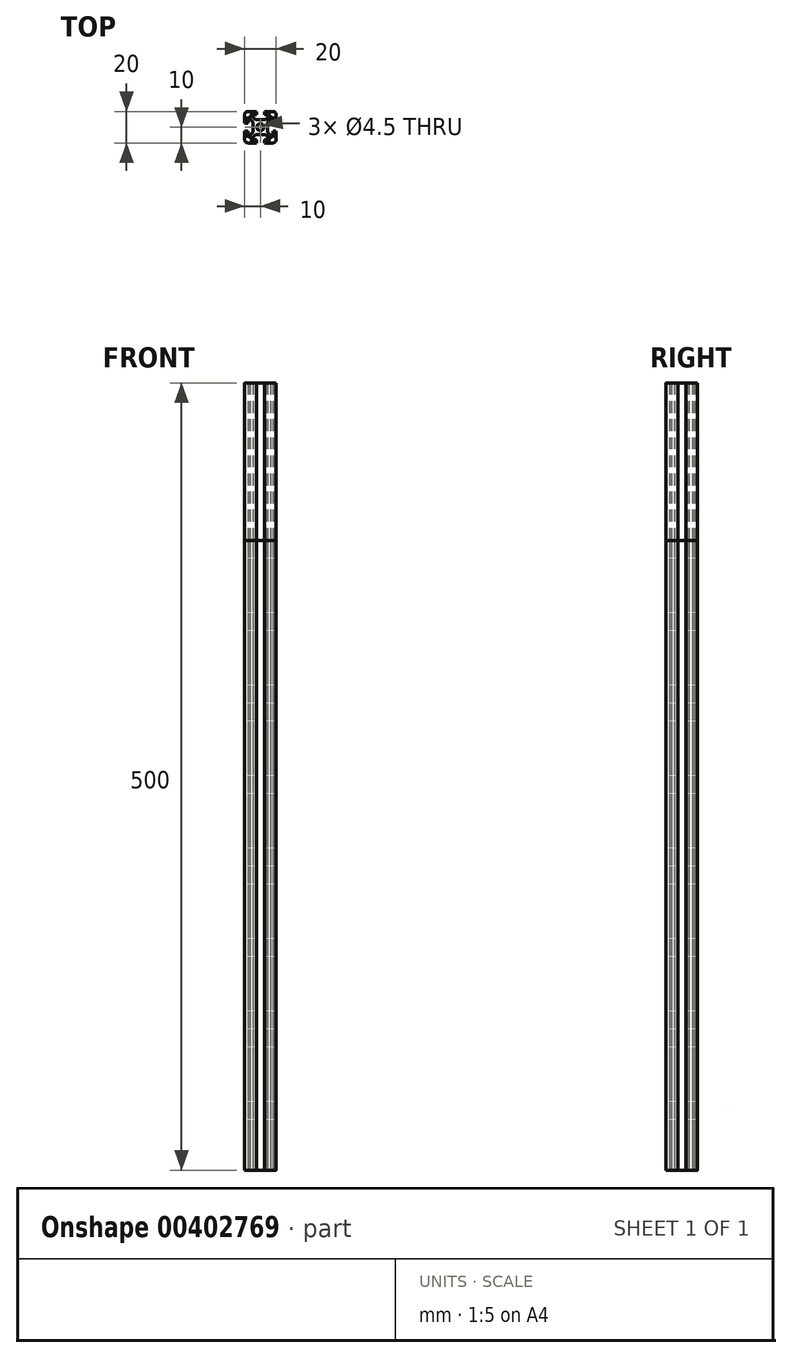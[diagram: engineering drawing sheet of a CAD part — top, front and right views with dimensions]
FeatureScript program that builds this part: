
annotation { "Feature Type Name" : "Feature", "Feature Type Description" : "" }
export const myFeature = defineFeature(function(context is Context, id is Id, definition is map)
    precondition{}
    {
        {
            var Q0;
            Q0=qCreatedBy(makeId("Top.planeOp"),FACE);
            var sketch = newSketch(context, id + "F0", { "sketchPlane" : qUnion([Q0])});
            skLineSegment(sketch, "E0.bottom", {"start": v(-8, -10) * mm, "end": v(-2.5, -10) * mm});
            skLineSegment(sketch, "E0.top", {"start": v(-8, 10) * mm, "end": v(-2.5, 10) * mm});
            skLineSegment(sketch, "E0.left", {"start": v(-10, -8) * mm, "end": v(-10, -2.5) * mm});
            skLineSegment(sketch, "E0.right", {"start": v(10, -8) * mm, "end": v(10, -2.5) * mm});
            skPoint(sketch, "E0.middle", {"position": v(0, 0) * mm});
            skCircle(sketch, "E1", {"center": v(0, 0) * mm, "radius": 2.25 * mm});
            skPoint(sketch, "E2.visualSharp", {"position": v(10, -10) * mm});
            skArc(sketch, "E2.filletArc", {"start": v(8, -10) * mm, "mid": v(9.41, -9.41) * mm, "end": v(10, -8) * mm});
            skPoint(sketch, "E3.visualSharp", {"position": v(10, 10) * mm});
            skArc(sketch, "E3.filletArc", {"start": v(10, 8) * mm, "mid": v(9.41, 9.41) * mm, "end": v(8, 10) * mm});
            skPoint(sketch, "E4.visualSharp", {"position": v(-10, 10) * mm});
            skArc(sketch, "E4.filletArc", {"start": v(-8, 10) * mm, "mid": v(-9.41, 9.41) * mm, "end": v(-10, 8) * mm});
            skPoint(sketch, "E5.visualSharp", {"position": v(-10, -10) * mm});
            skArc(sketch, "E5.filletArc", {"start": v(-10, -8) * mm, "mid": v(-9.41, -9.41) * mm, "end": v(-8, -10) * mm});
            skLineSegment(sketch, "E6", {"start": v(2.5, 10) * mm, "end": v(2.5, 8) * mm});
            skLineSegment(sketch, "E7", {"start": v(2.5, 8) * mm, "end": v(6.59, 8) * mm});
            skLineSegment(sketch, "E8", {"start": v(6.59, 8) * mm, "end": v(3.2, 4.62) * mm});
            skLineSegment(sketch, "E9", {"start": v(3.2, 4.62) * mm, "end": v(0, 4.62) * mm});
            skLineSegment(sketch, "E10.MirrorCS", {"start": v(-3.2, 4.62) * mm, "end": v(0, 4.62) * mm});
            skLineSegment(sketch, "E11.MirrorCS", {"start": v(-6.59, 8) * mm, "end": v(-3.2, 4.62) * mm});
            skLineSegment(sketch, "E12.MirrorCS", {"start": v(-2.5, 8) * mm, "end": v(-6.59, 8) * mm});
            skLineSegment(sketch, "E13.MirrorCS", {"start": v(-2.5, 10) * mm, "end": v(-2.5, 8) * mm});
            skLineSegment(sketch, "E14.1.0", {"start": v(-4.62, -3.2) * mm, "end": v(-4.62, 0) * mm});
            skLineSegment(sketch, "E14.1.1", {"start": v(-8, -6.59) * mm, "end": v(-4.62, -3.2) * mm});
            skLineSegment(sketch, "E14.1.2", {"start": v(-8, -2.5) * mm, "end": v(-8, -6.59) * mm});
            skLineSegment(sketch, "E14.1.3", {"start": v(-10, 2.5) * mm, "end": v(-8, 2.5) * mm});
            skLineSegment(sketch, "E14.1.4", {"start": v(-8, 2.5) * mm, "end": v(-8, 6.59) * mm});
            skLineSegment(sketch, "E14.1.5", {"start": v(-10, -2.5) * mm, "end": v(-8, -2.5) * mm});
            skLineSegment(sketch, "E14.1.6", {"start": v(-8, 6.59) * mm, "end": v(-4.62, 3.2) * mm});
            skLineSegment(sketch, "E14.1.7", {"start": v(-4.62, 3.2) * mm, "end": v(-4.62, 0) * mm});
            skLineSegment(sketch, "E14.2.0", {"start": v(3.2, -4.62) * mm, "end": v(0, -4.62) * mm});
            skLineSegment(sketch, "E14.2.1", {"start": v(6.59, -8) * mm, "end": v(3.2, -4.62) * mm});
            skLineSegment(sketch, "E14.2.2", {"start": v(2.5, -8) * mm, "end": v(6.59, -8) * mm});
            skLineSegment(sketch, "E14.2.3", {"start": v(-2.5, -10) * mm, "end": v(-2.5, -8) * mm});
            skLineSegment(sketch, "E14.2.4", {"start": v(-2.5, -8) * mm, "end": v(-6.59, -8) * mm});
            skLineSegment(sketch, "E14.2.5", {"start": v(2.5, -10) * mm, "end": v(2.5, -8) * mm});
            skLineSegment(sketch, "E14.2.6", {"start": v(-6.59, -8) * mm, "end": v(-3.2, -4.62) * mm});
            skLineSegment(sketch, "E14.2.7", {"start": v(-3.2, -4.62) * mm, "end": v(0, -4.62) * mm});
            skLineSegment(sketch, "E14.3.0", {"start": v(4.62, 3.2) * mm, "end": v(4.62, 0) * mm});
            skLineSegment(sketch, "E14.3.1", {"start": v(8, 6.59) * mm, "end": v(4.62, 3.2) * mm});
            skLineSegment(sketch, "E14.3.2", {"start": v(8, 2.5) * mm, "end": v(8, 6.59) * mm});
            skLineSegment(sketch, "E14.3.3", {"start": v(10, -2.5) * mm, "end": v(8, -2.5) * mm});
            skLineSegment(sketch, "E14.3.4", {"start": v(8, -2.5) * mm, "end": v(8, -6.59) * mm});
            skLineSegment(sketch, "E14.3.5", {"start": v(10, 2.5) * mm, "end": v(8, 2.5) * mm});
            skLineSegment(sketch, "E14.3.6", {"start": v(8, -6.59) * mm, "end": v(4.62, -3.2) * mm});
            skLineSegment(sketch, "E14.3.7", {"start": v(4.62, -3.2) * mm, "end": v(4.62, 0) * mm});
            skLineSegment(sketch, "E15.trimOffspring", {"start": v(2.5, 10) * mm, "end": v(8, 10) * mm});
            skLineSegment(sketch, "E16.trimOffspring", {"start": v(10, 2.5) * mm, "end": v(10, 8) * mm});
            skLineSegment(sketch, "E17.trimOffspring", {"start": v(2.5, -10) * mm, "end": v(8, -10) * mm});
            skLineSegment(sketch, "E18.trimOffspring", {"start": v(-10, 2.5) * mm, "end": v(-10, 8) * mm});
            skSolve(sketch);
        }
        {
            var Q0;
            Q0=makeQuery(id+"F0.imprint","IMPRINT",FACE,{"disambiguationData":[TD([[makeQuery(id+"F0.imprint","IMPRINT",EDGE,{"derivedFrom":sQuery(id+"F0.wireOp",EDGE,"E0.bottom")}),1.0]])]});
            extrude(context, id + "F1", {"entities" : qUnion([Q0]), "depth" : 500 * mm});
        }
        {
            var Q0;
            Q0=makeQuery(id+"F0.imprint","IMPRINT",FACE,{"disambiguationData":[TD([[makeQuery(id+"F0.imprint","IMPRINT",EDGE,{"derivedFrom":sQuery(id+"F0.wireOp",EDGE,"E0.bottom")}),1.0]])]});
            extrude(context, id + "F2", {"entities" : qUnion([Q0]), "depth" : 500 * mm});
        }
        {
            var Q0;
            Q0=makeQuery(id+"F0.imprint","IMPRINT",FACE,{"disambiguationData":[TD([[makeQuery(id+"F0.imprint","IMPRINT",EDGE,{"derivedFrom":sQuery(id+"F0.wireOp",EDGE,"E0.bottom")}),1.0]])]});
            extrude(context, id + "F3", {"entities" : qUnion([Q0]), "depth" : 400 * mm});
        }
    });
